# Revit family: Door-French-Pella-Architect_Series-Hinged_Patio_Door-InSwing-Sidelight
name_source: partatom
category: Doors
revit_build: Autodesk Revit Architecture 2013 (Build: 20130531_2115(x64)
units: mm (PartAtom-declared; Revit-internal decimal feet)

## types (5) — shared parameters
Analytic Construction = <None>
Architectural Design Manual = www.pellaadm.com
Construction Type = -
Cross Grille Pattern = No
Custom Grille Pattern = No
Custom Horizontal Lites = 2
Custom Vertical Lites = 6
DLO Width = 11 249/256"
Description = In-Swing - Sidelight Unit
Door Grille Visibility = Yes
Energy Efficiency = http://www.pella.com
Environmental Commitment = http://www.pella.com
Ext Finish = Aluminum - Pella - Brown
Function = Interior
Glazing Finish = Glass - Pella - Clear Insulating Glass
Glazing Thickness = 107/128"
Int Finish = Wood - Pella - Pine
Manufacturer = Pella - Windows & Doors
Note* = Maximum Frame Depth is 211 mm; if Wall Depth exceeds this value please recalculated Set Back to reflect
Operation = Sidelight
Prairie Grille Pattern = No
Product Documentation Link = http://media.pella.com
Product Name = Architect Series Hinged Patio Door
Product Page URL = http://www.pella.com
Rough Width = 1' - 6 3/4"
Series = Architect Series - Aluminum-Clad Wood
Top Row Grille Pattern = No
Traditional Grille Pattern = Yes
URL = www.pella.com
Unit Width = 1' - 3 191/256"
Wall Closure = By host
Width = 1' - 6"

## per-type parameters (varying)
| type | C Height | DLO Height | Height | Hinges | Rough Height | Unit Height |
| 1880 | 6' - 7 1/2" | 5' - 3 105/256" | 6' - 7 1/2" | 3 | 6' - 8" | 6' - 4 5/8" |
| 1881 | 6' - 8 1/8" | 5' - 4 9/256" | 6' - 8 1/8" | 3 | 6' - 8 5/8" | 6' - 5 1/4" |
| 1882 | 6' - 9 1/2" | 5' - 5 105/256" | 6' - 9 1/2" | 3 | 6' - 10" | 6' - 6 5/8" |
| 1886 | 7' - 2" | 5' - 9 233/256" | 7' - 2" | 4 | 7' - 2 1/2" | 6' - 11 1/8" |
| 1896 | 7' - 11 1/2" | 6' - 7 105/256" | 7' - 11 1/2" | 4 | 8' - 0" | 7' - 8 5/8" |

note: column(s) folded — value = type name in every type: Model

## geometry (parser evidence)
native form markers: Blend x6, Sweep x10
no freeform markers — native parametric forms only
